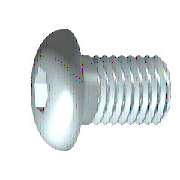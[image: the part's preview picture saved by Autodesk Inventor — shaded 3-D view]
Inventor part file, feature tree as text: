
AUTODESK INVENTOR PART (.ipt)
format: ipt  version: 2015 (Build 190159000, 159)  size: 201,728 bytes
history: native  units: mm (DEFAULTED — no unit token found)
features: sketch x2, extrude x1, plane x1, fillet x1
ambient origin geometry x7: Origin, YZ Plane, XY Plane, X Axis, Y Axis, Z Axis, Center Point
bodies: Solid1 (feature_tree), Body (feature_tree)
feature tree (5):
  extrude  "Slot"  Depth=3.3528mm
  plane  "Work Plane1"
  fillet  "Fillet2"  Radius=3.3528mm
  sketch  "Sketch1"  dims[d1=13.3348mm d2=2.5401mm d3=3.3528mm]
  sketch  "Sketch2"  dims[d4=2.2098mm d5=60.0deg d6=6.35mm d7=6.35mm d8=4.575385mm d9=11.0998mm d10=90.0deg d11=10.0mm d12=0.0mm d13=13.3348mm d14=0.0mm d15=0.779018mm d16=0.779018mm d17=2.9718mm d19=0.0mm d26=15.875mm d27=45.0deg d28=0.0mm d29=0.0mm d30=0.1mm]
